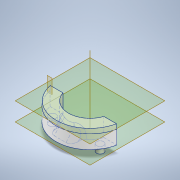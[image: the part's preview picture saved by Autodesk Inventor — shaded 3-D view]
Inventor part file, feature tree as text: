
AUTODESK INVENTOR PART (.ipt)
format: ipt  version: 2021 (Build 250183000, 183)  size: 519,680 bytes
history: native  units: in
note: dims shown in document units (in); Inventor stores cm internally (conversion verified against a paired STEP export)
features: sketch x10, extrude x9, plane x3, fillet x2, other x1, revolve x1, pattern_circular x1, mirror x1, chamfer x1
ambient origin geometry x8: Origin, YZ Plane, XZ Plane, XY Plane, X Axis, Y Axis, Z Axis, Center Point
bodies: Solid1 (feature_tree)
feature tree (29):
  extrude  "Extrusion1"  Depth=1.0236in
  other  "Work Axis1"
  revolve  "Revolution1"  [1 undecoded]
  extrude  "Extrusion2"  Depth=1.0079in
  extrude  "Extrusion3"  TaperAngle=90.0deg  [1 undecoded]
  extrude  "Extrusion4"  Depth=0.8976in
  extrude  "Extrusion5"  Depth=1.0236in TaperAngle=0.0deg
  pattern_circular  "Circular Pattern1"  Count=5 Angle=240.0deg
  mirror  "Mirror1"
  fillet  "Fillet2"  Radius=0.5039in
  extrude  "Extrusion7"  Depth=0.3937in
  chamfer  "Chamfer2"  Distance=0.6693in
  fillet  "Fillet3"  Radius=0.3937in
  plane  "Work Plane1"
  extrude  "Extrusion8"  Depth=0.3937in
  plane  "Work Plane2"
  extrude  "Extrusion10"  Depth=0.3937in
  plane  "Work Plane3"
  extrude  "Extrusion11"  Depth=0.3937in TaperAngle=0.0deg
  sketch  "Sketch1"  dims[d0=2.0472in d1=1.0236in]
  sketch  "Sketch2"  dims[d2=1.0236in d3=1.0236in]
  sketch  "Sketch3"  dims[d4=1.378in d5=0.0in d6=1.0079in]
  sketch  "Sketch4"  dims[d7=90.0deg d8=90.0deg]
  sketch  "Sketch5"  dims[d9=0.0394in d10=0.0in d11=0.8976in]
  sketch  "Sketch8"  dims[d12=0.0in d13=0.0in d14=1.0236in d15=0.0in]
  sketch  "Sketch10"  dims[d16=1.2913in]
  sketch  "Sketch11"  dims[d21=0.2126in]
  sketch  "Sketch13"  dims[d22=0.8268in]
  sketch  "Sketch14"  dims[d23=0.1969in d24=0.0in d25=1.9685in d26=240.0deg d33=0.5039in d34=0.0394in d35=0.6693in d36=0.3937in d37=0.3346in d38=0.126in d39=0.3937in d40=0.0in d41=0.3937in d42=0.3386in d43=45.0deg d44=0.1575in d45=-0.5512in d46=0.0in d47=0.0in d48=0.0in d51=0.3937in d52=0.0in d53=0.1969in d54=0.0in d55=0.0in]
note: 2 required parameter values undecoded (feature->parameter linkage not recoverable at this tier; creation-order binding heuristic only, values carry confidence <= 0.55)